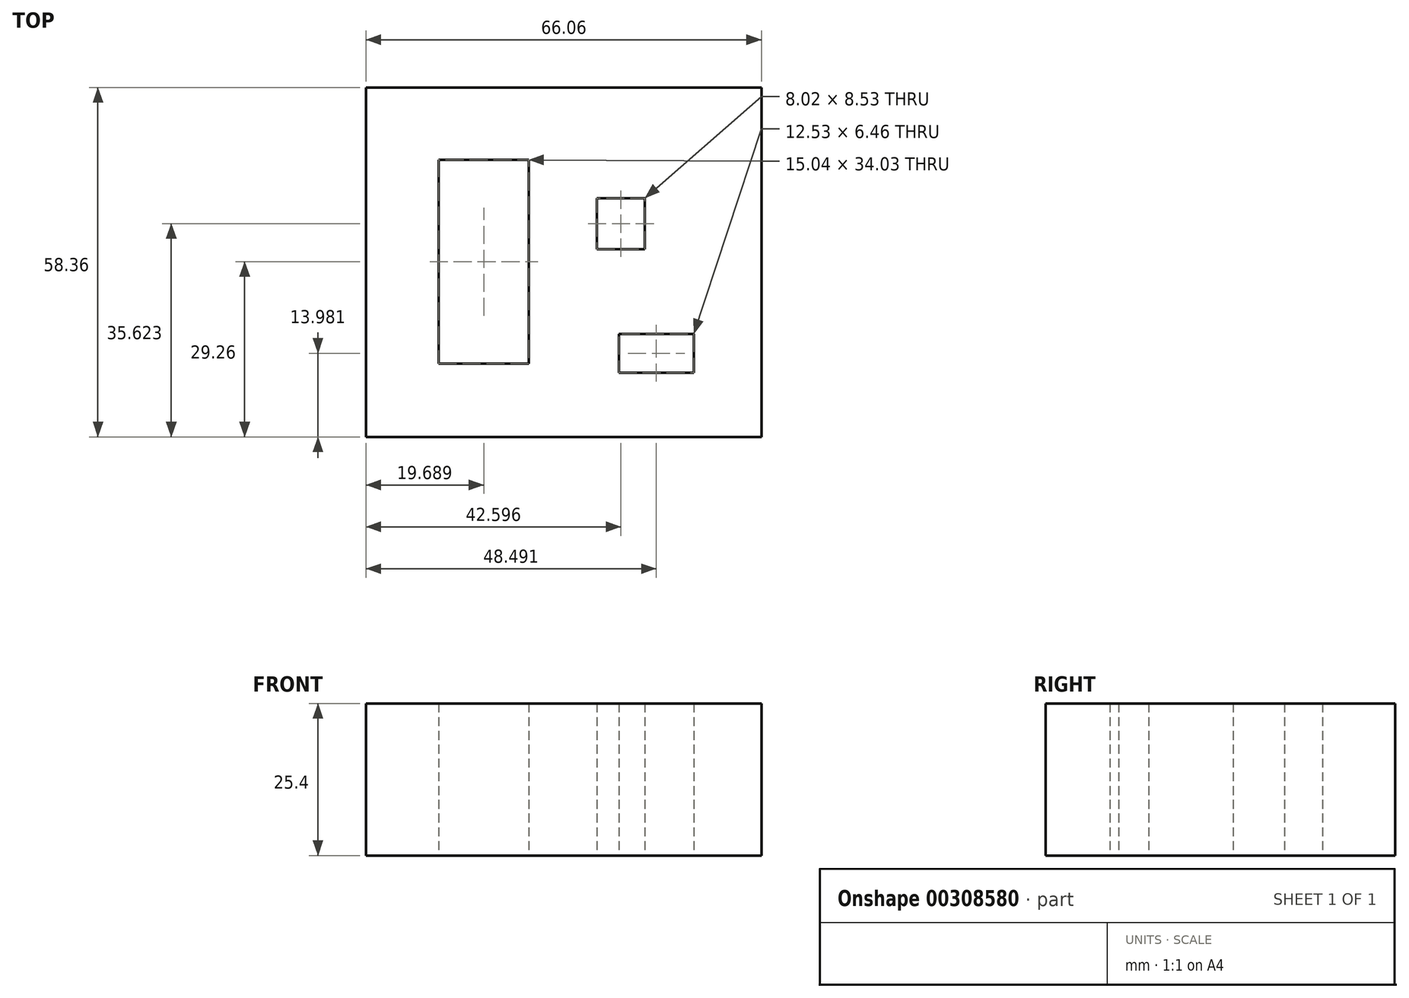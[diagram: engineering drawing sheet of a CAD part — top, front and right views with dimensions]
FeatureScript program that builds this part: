
annotation { "Feature Type Name" : "Feature", "Feature Type Description" : "" }
export const myFeature = defineFeature(function(context is Context, id is Id, definition is map)
    precondition{}
    {
        {
            var Q0;
            Q0=qCreatedBy(makeId("Top.planeOp"),FACE);
            var sketch = newSketch(context, id + "F0", { "sketchPlane" : qUnion([Q0])});
            skLineSegment(sketch, "E0.bottom", {"start": v(-27.2, -31.36) * mm, "end": v(38.85, -31.36) * mm});
            skLineSegment(sketch, "E0.top", {"start": v(-27.2, 27) * mm, "end": v(38.85, 27) * mm});
            skLineSegment(sketch, "E0.left", {"start": v(-27.2, -31.36) * mm, "end": v(-27.2, 27) * mm});
            skLineSegment(sketch, "E0.right", {"start": v(38.85, -31.36) * mm, "end": v(38.85, 27) * mm});
            skLineSegment(sketch, "E1.bottom", {"start": v(-15.04, -19.12) * mm, "end": v(0, -19.12) * mm});
            skLineSegment(sketch, "E1.top", {"start": v(-15.04, 14.92) * mm, "end": v(0, 14.92) * mm});
            skLineSegment(sketch, "E1.left", {"start": v(-15.04, -19.12) * mm, "end": v(-15.04, 14.92) * mm});
            skLineSegment(sketch, "E1.right", {"start": v(0, -19.12) * mm, "end": v(0, 14.92) * mm});
            skLineSegment(sketch, "E2.bottom", {"start": v(11.38, 8.52) * mm, "end": v(19.4, 8.52) * mm});
            skLineSegment(sketch, "E2.top", {"start": v(11.38, 0) * mm, "end": v(19.4, 0) * mm});
            skLineSegment(sketch, "E2.left", {"start": v(11.38, 8.52) * mm, "end": v(11.38, 0) * mm});
            skLineSegment(sketch, "E2.right", {"start": v(19.4, 8.52) * mm, "end": v(19.4, 0) * mm});
            skLineSegment(sketch, "E3.bottom", {"start": v(15.02, -14.15) * mm, "end": v(27.55, -14.15) * mm});
            skLineSegment(sketch, "E3.top", {"start": v(15.02, -20.6) * mm, "end": v(27.55, -20.6) * mm});
            skLineSegment(sketch, "E3.left", {"start": v(15.02, -14.15) * mm, "end": v(15.02, -20.6) * mm});
            skLineSegment(sketch, "E3.right", {"start": v(27.55, -14.15) * mm, "end": v(27.55, -20.6) * mm});
            skSolve(sketch);
        }
        {
            var Q0;
            Q0=makeQuery(id+"F0.imprint","IMPRINT",FACE,{"disambiguationData":[TD([[makeQuery(id+"F0.imprint","IMPRINT",EDGE,{"derivedFrom":sQuery(id+"F0.wireOp",EDGE,"E0.bottom")}),1.0]])]});
            extrude(context, id + "F1", {"entities" : qUnion([Q0]), "depth" : 25.4 * mm});
        }
    });
